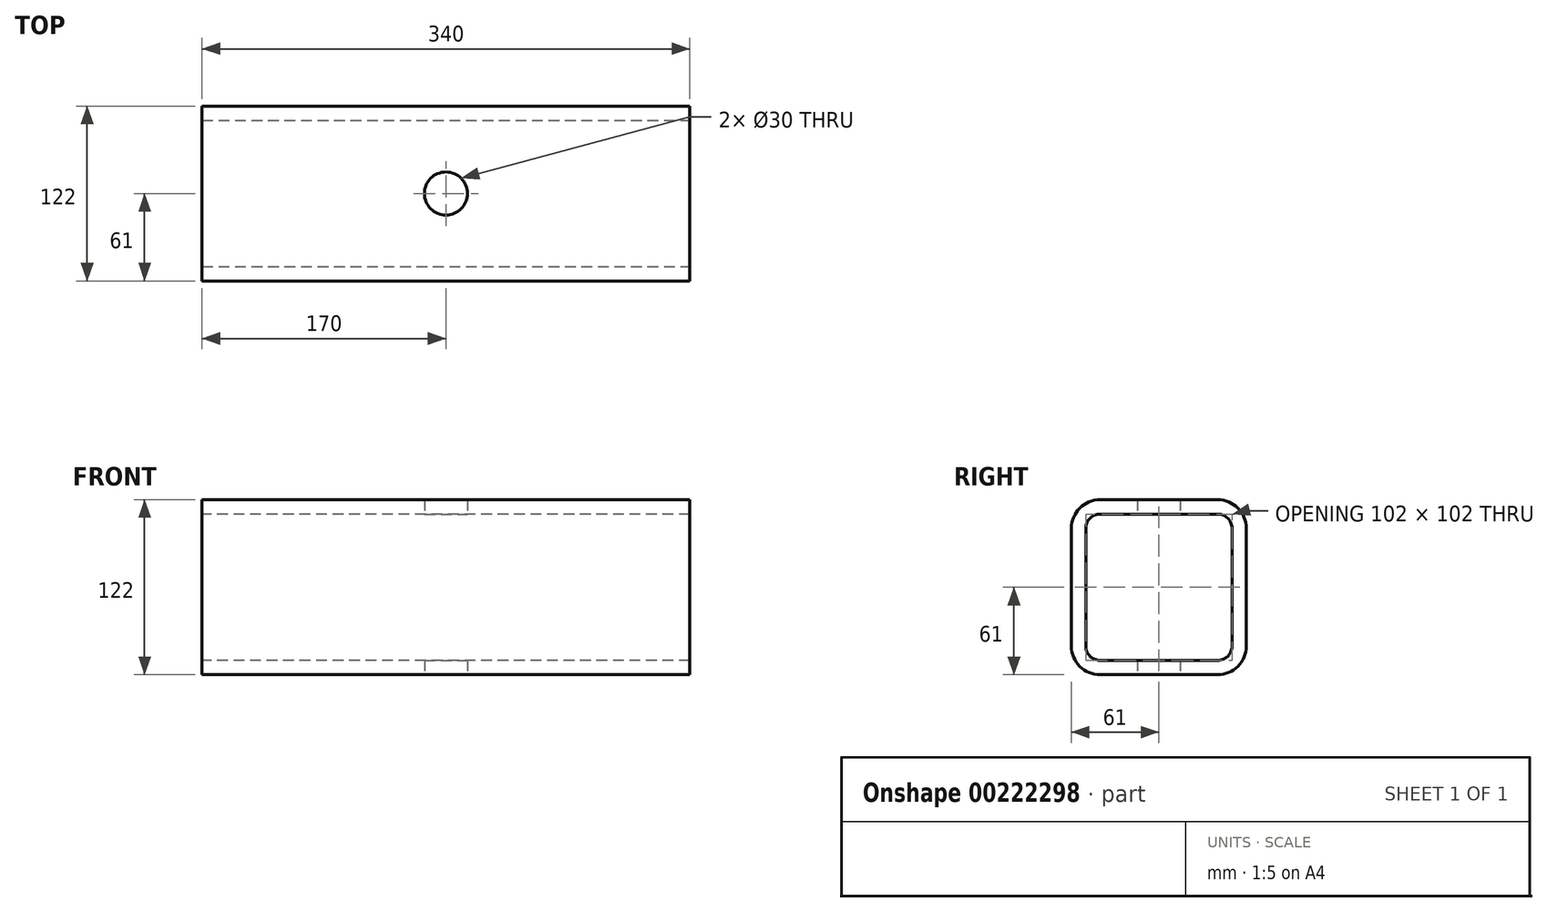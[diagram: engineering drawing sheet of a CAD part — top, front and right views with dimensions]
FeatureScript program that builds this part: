
annotation { "Feature Type Name" : "Feature", "Feature Type Description" : "" }
export const myFeature = defineFeature(function(context is Context, id is Id, definition is map)
    precondition{}
    {
        {
            var Q0;
            Q0=qCreatedBy(makeId("Front.planeOp"),FACE);
            var sketch = newSketch(context, id + "F0", { "sketchPlane" : qUnion([Q0])});
            skLineSegment(sketch, "E0.bottom", {"start": v(170, -61) * mm, "end": v(-170, -61) * mm});
            skLineSegment(sketch, "E0.top", {"start": v(170, 61) * mm, "end": v(-170, 61) * mm});
            skLineSegment(sketch, "E0.left", {"start": v(170, -61) * mm, "end": v(170, 61) * mm});
            skLineSegment(sketch, "E0.right", {"start": v(-170, -61) * mm, "end": v(-170, 61) * mm});
            skPoint(sketch, "E0.middle", {"position": v(0, 0) * mm});
            skPoint(sketch, "E1.visualSharp", {"position": v(-170, 61) * mm});
            skSolve(sketch);
        }
        {
            var Q0;
            Q0 = qSketchRegion(id + "F0", true);
            extrude(context, id + "F1", {"entities" : qUnion([Q0]), "depth" : 122 * mm, "offsetDistance" : 25 * mm, "symmetric" : true});
        }
        {
            var Q0;
            Q0=makeQuery(id+"F1.opExtrude","CAP_EDGE",EDGE,{"disambiguationData":[OSD([sQuery(id+"F0.wireOp",EDGE,"E0.top")])],"isStart":true});
            var Q1;
            Q1=makeQuery(id+"F1.opExtrude","CAP_EDGE",EDGE,{"disambiguationData":[OSD([sQuery(id+"F0.wireOp",EDGE,"E0.top")])],"isStart":false});
            var Q2;
            Q2=makeQuery(id+"F1.opExtrude","CAP_EDGE",EDGE,{"disambiguationData":[OSD([sQuery(id+"F0.wireOp",EDGE,"E0.bottom")])],"isStart":true});
            var Q3;
            Q3=makeQuery(id+"F1.opExtrude","CAP_EDGE",EDGE,{"disambiguationData":[OSD([sQuery(id+"F0.wireOp",EDGE,"E0.bottom")])],"isStart":false});
            fillet(context, id + "F2", {"entities" : qUnion([Q0, Q1, Q2, Q3]), "radius" : 20 * mm, "tangentPropagation" : true, "allowEdgeOverflow" : false});
        }
        {
            var Q0;
            Q0=makeQuery(id+"F1.opExtrude","SWEPT_FACE",FACE,{"disambiguationData":[OSD([sQuery(id+"F0.wireOp",EDGE,"E0.left")])]});
            var Q1;
            Q1=makeQuery(id+"F1.opExtrude","SWEPT_FACE",FACE,{"disambiguationData":[OSD([sQuery(id+"F0.wireOp",EDGE,"E0.right")])]});
            shell(context, id + "F3", {"entities" : qUnion([Q0, Q1]), "thickness" : 10 * mm});
        }
        {
            var Q0;
            Q0=qCreatedBy(makeId("Top.planeOp"),FACE);
            var sketch = newSketch(context, id + "F4", { "sketchPlane" : qUnion([Q0])});
            skCircle(sketch, "E2", {"center": v(0, 0) * mm, "radius": 15 * mm});
            skSolve(sketch);
        }
        {
            var Q0;
            Q0 = qSketchRegion(id + "F4", true);
            extrude(context, id + "F5", {"entities" : qUnion([Q0]), "operationType" : NewBodyOperationType.REMOVE, "endBound" : BoundingType.THROUGH_ALL, "depth" : 25 * mm, "offsetDistance" : 25 * mm, "hasSecondDirection" : true, "secondDirectionBound" : BoundingType.THROUGH_ALL, "secondDirectionOppositeDirection" : true, "secondDirectionDepth" : 25 * mm});
        }
    });
